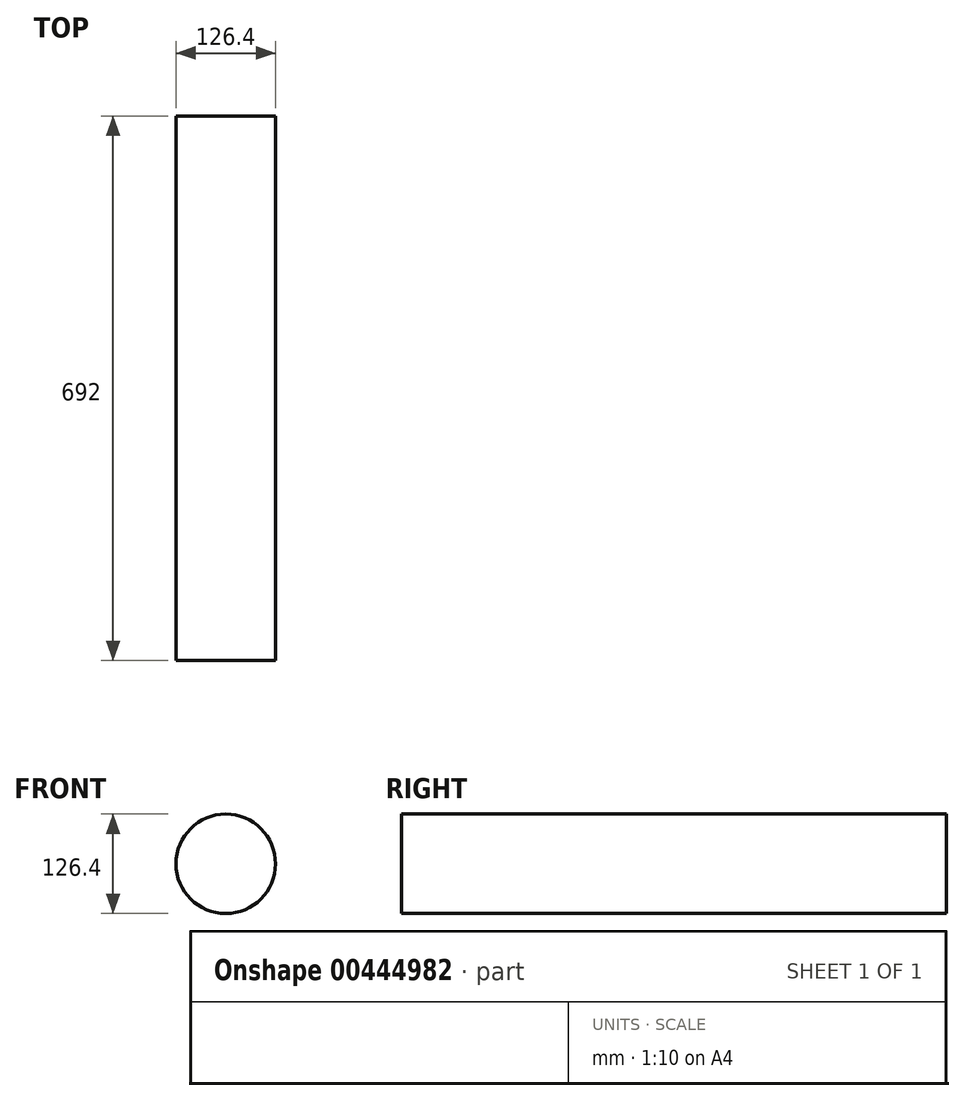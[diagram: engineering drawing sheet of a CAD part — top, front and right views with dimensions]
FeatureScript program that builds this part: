
annotation { "Feature Type Name" : "Feature", "Feature Type Description" : "" }
export const myFeature = defineFeature(function(context is Context, id is Id, definition is map)
    precondition{}
    {
        {
            var Q0;
            Q0=qCreatedBy(makeId("Top.planeOp"),FACE);
            var sketch = newSketch(context, id + "F0", { "sketchPlane" : qUnion([Q0])});
            skLineSegment(sketch, "E0", {"start": v(10.64, 0) * mm, "end": v(10.64, 692) * mm});
            skLineSegment(sketch, "E1", {"start": v(10.64, 692) * mm, "end": v(73.84, 692) * mm});
            skLineSegment(sketch, "E2", {"start": v(73.84, 692) * mm, "end": v(73.84, 0) * mm});
            skLineSegment(sketch, "E3", {"start": v(73.84, 0) * mm, "end": v(10.64, 0) * mm});
            skSolve(sketch);
        }
        {
            var Q0;
            Q0=makeQuery(id+"F0.imprint","IMPRINT",FACE,{"disambiguationData":[TD([[makeQuery(id+"F0.imprint","IMPRINT",EDGE,{"derivedFrom":sQuery(id+"F0.wireOp",EDGE,"E0")}),-1.0]])]});
            var Q1;
            Q1=sQuery(id+"F0.wireOp",EDGE,"E2");
            revolve(context, id + "F1", {"entities" : qUnion([Q0]), "axis" : qUnion([Q1]), "revolveType" : RevolveType.FULL});
        }
    });
